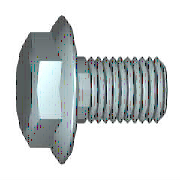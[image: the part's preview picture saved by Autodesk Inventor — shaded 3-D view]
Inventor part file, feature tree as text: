
AUTODESK INVENTOR PART (.ipt)
format: ipt  version: 2018 (Build 220112000, 112)  size: 212,992 bytes
history: native  units: mm (DEFAULTED — no unit token found)
features: sketch x3, other x2, extrude x1, plane x1
ambient origin geometry x7: Origin, YZ Plane, XZ Plane, X Axis, Y Axis, Z Axis, Center Point
bodies: Solid1 (feature_tree)
feature tree (7):
  other  "Corpo"
  extrude  "Testa"  Depth=1.1mm
  other  "Smusso1"
  plane  "Work Plane1"
  sketch  "Schizzo1"
  sketch  "Schizzo2"
  sketch  "Schizzo3"
